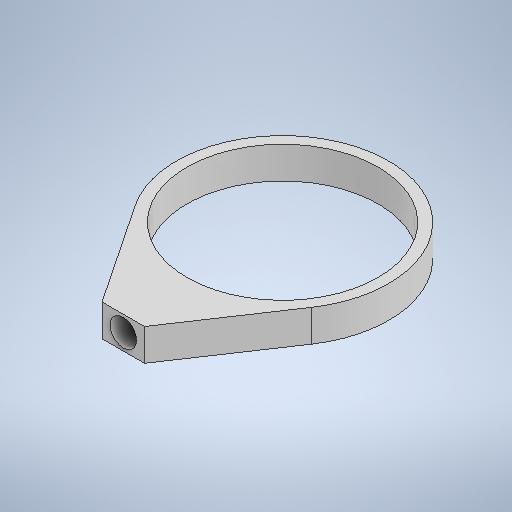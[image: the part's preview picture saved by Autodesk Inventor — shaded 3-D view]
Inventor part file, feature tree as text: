
AUTODESK INVENTOR PART (.ipt)
format: ipt  version: 2025.1 (Build 291241000, 241)  size: 281,088 bytes
history: native  units: mm
features: extrude x3, sketch x3
ambient origin geometry x8: Origin, YZ Plane, XZ Plane, XY Plane, X Axis, Y Axis, Z Axis, Center Point
bodies: Solid1 (feature_tree)
feature tree (6):
  extrude  "Extrusion1"  Depth=4.0mm
  extrude  "Extrusion2"  Depth=3.0mm TaperAngle=0.0deg
  extrude  "Extrusion3"  Depth=3.0mm TaperAngle=0.0deg
  sketch  "Sketch1"  dims[d0=20.0mm d1=4.0mm]
  sketch  "Sketch2"  dims[d2=15.0mm d3=3.0mm d4=0.0mm]
  sketch  "Sketch3"  dims[d5=18.0mm d6=3.0mm d7=0.0mm d8=2.5mm d9=3.0mm d10=0.0mm]
